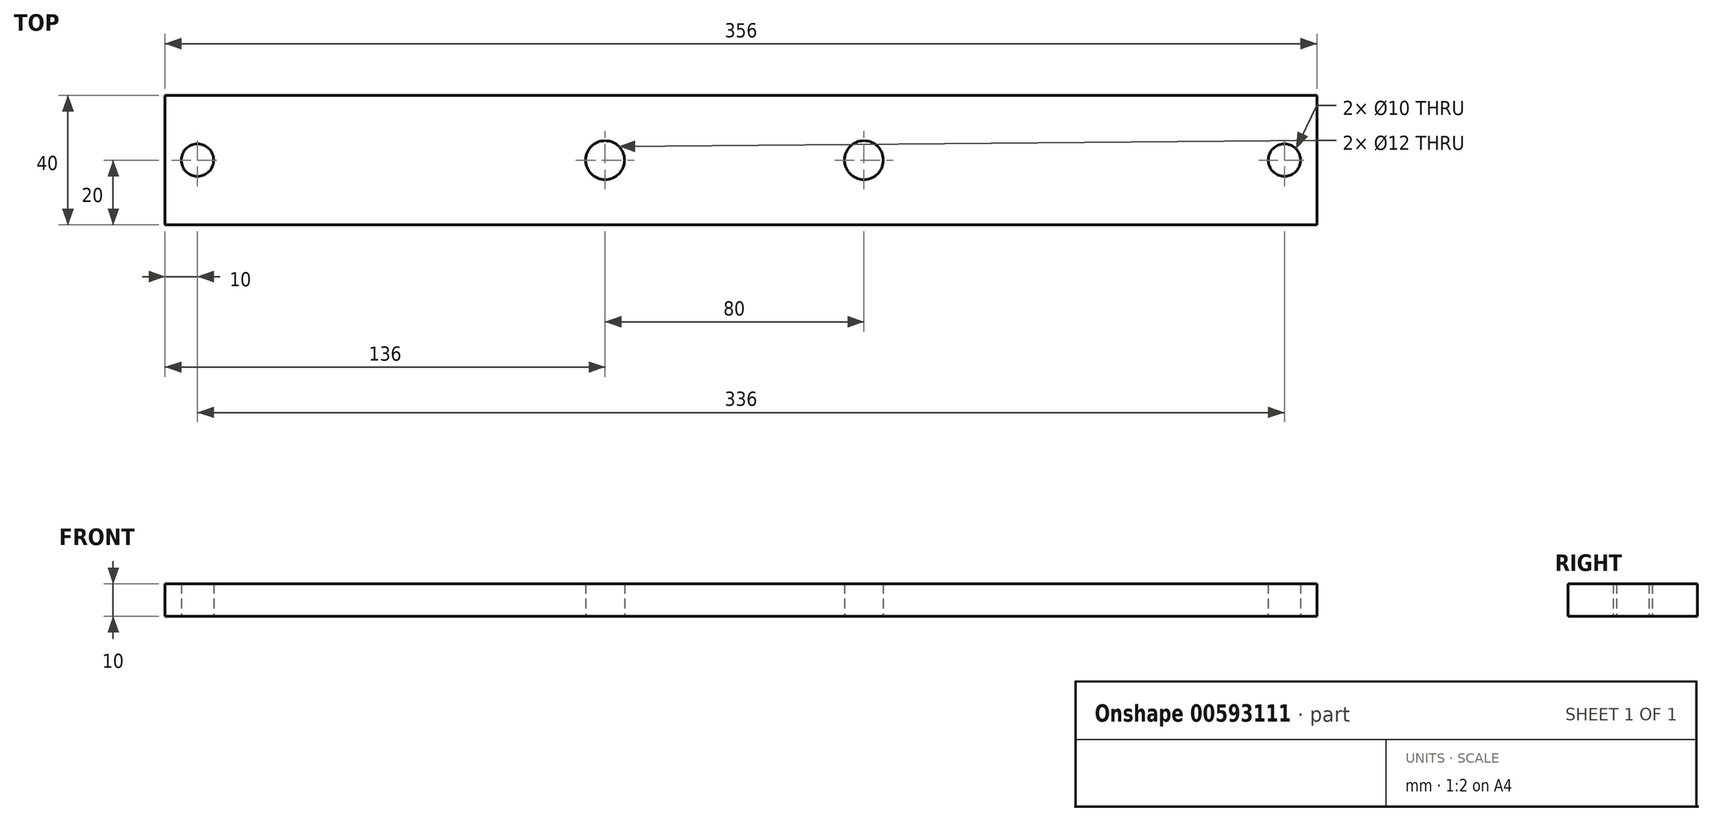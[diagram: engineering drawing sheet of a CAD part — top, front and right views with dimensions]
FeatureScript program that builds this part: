
annotation { "Feature Type Name" : "Feature", "Feature Type Description" : "" }
export const myFeature = defineFeature(function(context is Context, id is Id, definition is map)
    precondition{}
    {
        {
            var Q0;
            Q0=qCreatedBy(makeId("Top.planeOp"),FACE);
            var sketch = newSketch(context, id + "F0", { "sketchPlane" : qUnion([Q0])});
            skLineSegment(sketch, "E0.bottom", {"start": v(-178, -20) * mm, "end": v(178, -20) * mm});
            skLineSegment(sketch, "E0.top", {"start": v(-178, 20) * mm, "end": v(178, 20) * mm});
            skLineSegment(sketch, "E0.left", {"start": v(-178, -20) * mm, "end": v(-178, 20) * mm});
            skLineSegment(sketch, "E0.right", {"start": v(178, -20) * mm, "end": v(178, 20) * mm});
            skPoint(sketch, "E0.middle", {"position": v(0, 0) * mm});
            skCircle(sketch, "E1", {"center": v(-42, 0) * mm, "radius": 6 * mm});
            skCircle(sketch, "E2", {"center": v(38, 0) * mm, "radius": 6 * mm});
            skCircle(sketch, "E3", {"center": v(168, 0) * mm, "radius": 5 * mm});
            skCircle(sketch, "E4", {"center": v(-168, 0) * mm, "radius": 5 * mm});
            skLineSegment(sketch, "E5", {"start": v(-168, 0) * mm, "end": v(-42, 0) * mm, "construction": true});
            skLineSegment(sketch, "E6", {"start": v(38, 0) * mm, "end": v(168, 0) * mm, "construction": true});
            skSolve(sketch);
        }
        {
            var Q0;
            Q0=qSketchRegion(id+"F0",true);
            extrude(context, id + "F1", {"entities" : qUnion([Q0]), "depth" : 10 * mm, "offsetDistance" : 25 * mm});
        }
    });
